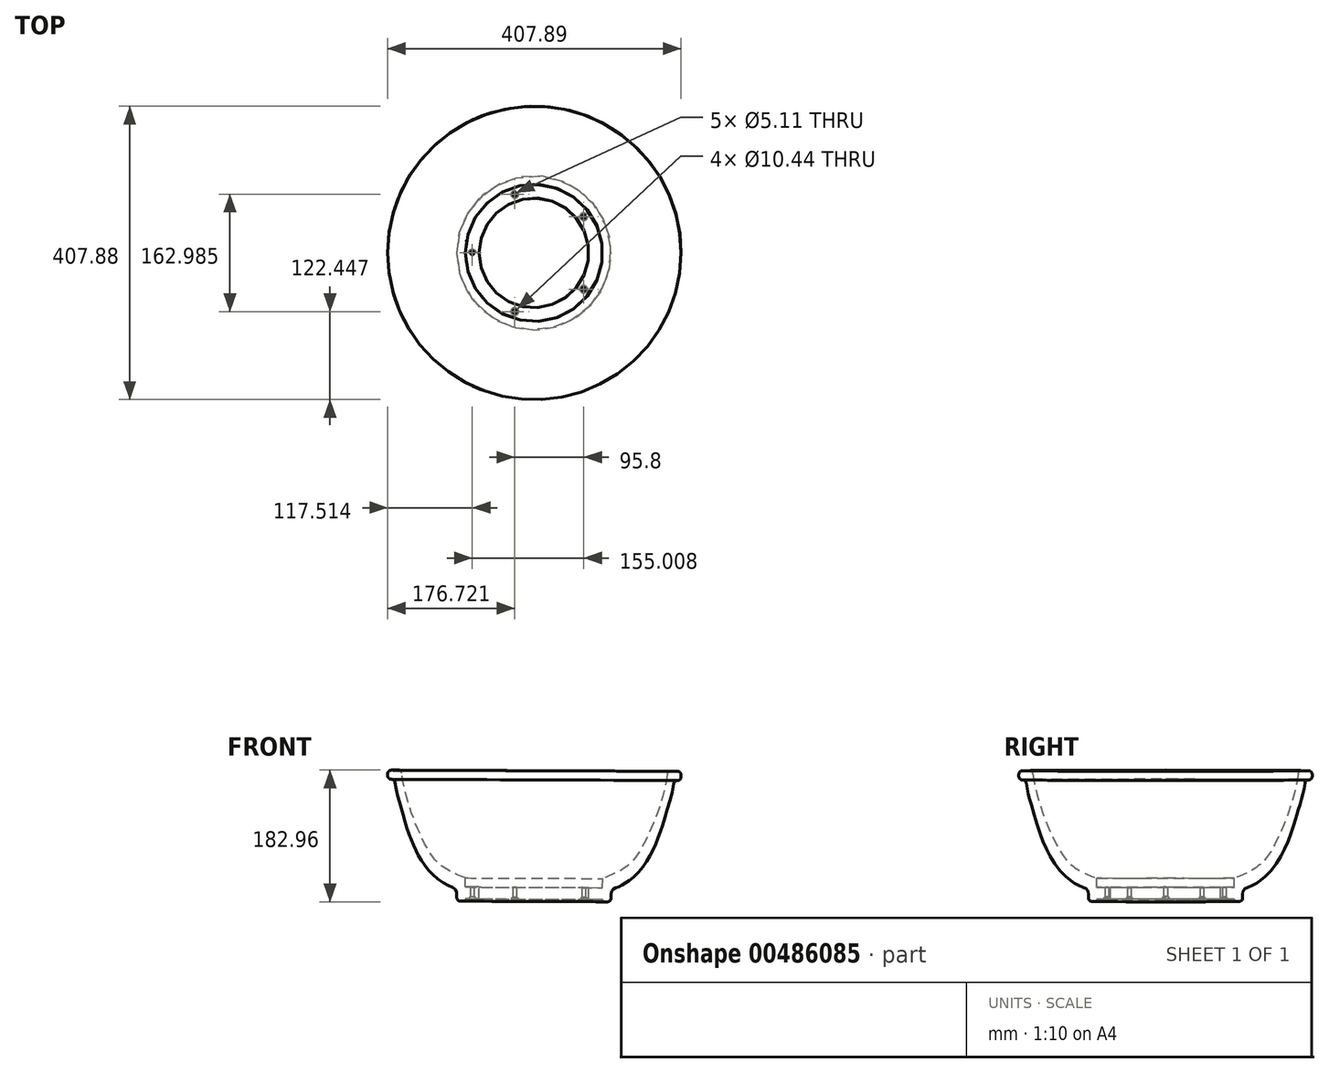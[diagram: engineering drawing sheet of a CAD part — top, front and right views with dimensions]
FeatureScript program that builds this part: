
annotation { "Feature Type Name" : "Feature", "Feature Type Description" : "" }
export const myFeature = defineFeature(function(context is Context, id is Id, definition is map)
    precondition{}
    {
        {
            var Q0;
            Q0=qCreatedBy(makeId("Front.planeOp"),FACE);
            var sketch = newSketch(context, id + "F0", { "sketchPlane" : qUnion([Q0])});
            skLineSegment(sketch, "E0", {"start": v(0, 0) * mm, "end": v(-114.3, 0) * mm, "construction": true});
            skLineSegment(sketch, "E1", {"start": v(0, 0) * mm, "end": v(1.53, 4.69) * mm, "construction": true});
            skLineSegment(sketch, "E2", {"start": v(0, 0) * mm, "end": v(0.77, 180.97) * mm, "construction": true});
            skPoint(sketch, "E2.endSnap0", {"position": v(0.77, 2.34) * mm});
            skLineSegment(sketch, "E3", {"start": v(-76.2, 0) * mm, "end": v(-76.2, 12.7) * mm, "construction": true});
            skLineSegment(sketch, "E4", {"start": v(0.77, 180.97) * mm, "end": v(-177.03, 181.73) * mm, "construction": true});
            skLineSegment(sketch, "E5", {"start": v(-177.03, 181.73) * mm, "end": v(-196.08, 181.73) * mm, "construction": true});
            skLineSegment(sketch, "E6", {"start": v(-196.08, 181.73) * mm, "end": v(-196.08, 169.03) * mm, "construction": true});
            skLineSegment(sketch, "E7", {"start": v(-196.08, 169.03) * mm, "end": v(-186.43, 169.03) * mm, "construction": true});
            skSolve(sketch);
        }
        {
            var Q0;
            Q0=qCreatedBy(makeId("Front.planeOp"),FACE);
            var sketch = newSketch(context, id + "F1", { "sketchPlane" : qUnion([Q0])});
            skLineSegment(sketch, "E8", {"start": v(-76.2, 0) * mm, "end": v(-76.2, 19.05) * mm});
            skLineSegment(sketch, "E9", {"start": v(-76.2, 19.05) * mm, "end": v(-95.25, 19.05) * mm});
            skLineSegment(sketch, "E10", {"start": v(-95.25, 19.05) * mm, "end": v(-95.25, 31.75) * mm});
            skLineSegment(sketch, "E11", {"start": v(-76.2, 0) * mm, "end": v(0, 0) * mm, "construction": true});
            skFitSpline(sketch, "E12", {"points": [v(-95.25, 31.75) * mm, v(-124, 45.57) * mm, v(-142.38, 63.68) * mm, v(-157, 90.58) * mm, v(-171.8, 127.39) * mm, v(-184.15, 181.6) * mm], "startDerivative": vector(-110.55, 41.42) * mm, "endDerivative": vector(-27.24, 248.45) * mm});
            skLineSegment(sketch, "E13", {"start": v(-184.15, 181.6) * mm, "end": v(-203.2, 181.6) * mm});
            skLineSegment(sketch, "E14", {"start": v(-203.2, 181.6) * mm, "end": v(-203.2, 168.9) * mm});
            skLineSegment(sketch, "E15", {"start": v(-203.2, 168.9) * mm, "end": v(-193.55, 168.9) * mm});
            skFitSpline(sketch, "E16", {"points": [v(-107.95, -0.5) * mm, v(-107.95, 14.65) * mm, v(-118.56, 20.96) * mm, v(-145.31, 41.35) * mm, v(-162.26, 66.76) * mm, v(-173.6, 93.1) * mm, v(-185.14, 131) * mm, v(-193.55, 168.9) * mm], "startDerivative": vector(19.18, 91.75) * mm, "endDerivative": vector(-30.73, 264.01) * mm});
            skLineSegment(sketch, "E17", {"start": v(-107.95, -0.5) * mm, "end": v(-95.25, -0.5) * mm});
            skLineSegment(sketch, "E18", {"start": v(-95.25, -0.5) * mm, "end": v(-95.25, 2.75) * mm});
            skLineSegment(sketch, "E19", {"start": v(-95.25, 2.75) * mm, "end": v(-76.2, 2.75) * mm});
            skLineSegment(sketch, "E20", {"start": v(0, 0) * mm, "end": v(0, 5.55) * mm, "construction": true});
            skLineSegment(sketch, "E21", {"start": v(0, 0) * mm, "end": v(0, 186.95) * mm, "construction": true});
            skPoint(sketch, "E22", {"position": v(0, 31.75) * mm});
            skSolve(sketch);
        }
        {
            var Q0;
            Q0=makeQuery(id+"F1.imprint","IMPRINT",FACE,{"disambiguationData":[TD([[makeQuery(id+"F1.imprint","IMPRINT",EDGE,{"derivedFrom":sQuery(id+"F1.wireOp",EDGE,"E8")}),1.0]])]});
            var Q1;
            Q1=sQuery(id+"F0.wireOp",EDGE,"E2");
            revolve(context, id + "F2", {"entities" : qUnion([Q0]), "axis" : qUnion([Q1]), "revolveType" : RevolveType.FULL});
        }
        {
            var Q0;
            Q0=makeQuery(id+"F2.opRevolve","SWEPT_EDGE",EDGE,{"disambiguationData":[OSD([sQuery(id+"F1.wireOp",EDGE,"E13"),sQuery(id+"F1.wireOp",EDGE,"E14")])]});
            var Q1;
            Q1=makeQuery(id+"F2.opRevolve","SWEPT_EDGE",EDGE,{"disambiguationData":[OSD([sQuery(id+"F1.wireOp",EDGE,"E14"),sQuery(id+"F1.wireOp",EDGE,"E15")])]});
            var Q2;
            Q2=makeQuery(id+"F2.opRevolve","SWEPT_EDGE",EDGE,{"disambiguationData":[OSD([sQuery(id+"F1.wireOp",EDGE,"E12"),sQuery(id+"F1.wireOp",EDGE,"E13")])]});
            var Q3;
            Q3=makeQuery(id+"F2.opRevolve","SWEPT_EDGE",EDGE,{"disambiguationData":[OSD([sQuery(id+"F1.wireOp",EDGE,"E15"),sQuery(id+"F1.wireOp",EDGE,"E16")])]});
            fillet(context, id + "F3", {"entities" : qUnion([Q0, Q1, Q2, Q3]), "radius" : 5.08 * mm, "tangentPropagation" : true, "allowEdgeOverflow" : false});
        }
        {
            var Q0;
            Q0=makeQuery(id+"F2.opRevolve","SWEPT_EDGE",EDGE,{"disambiguationData":[OSD([sQuery(id+"F1.wireOp",EDGE,"yEywBuH0-BsC1-ELP2-RhLg-4a1Xm9qmPdDr"),sQuery(id+"F1.wireOp",EDGE,"E16")])]});
            fillet(context, id + "F4", {"entities" : qUnion([Q0]), "radius" : 5.08 * mm, "tangentPropagation" : true, "allowEdgeOverflow" : false});
        }
        {
            var Q0;
            Q0=qCreatedBy(makeId("Top.planeOp"),FACE);
            var sketch = newSketch(context, id + "F5", { "sketchPlane" : qUnion([Q0])});
            skCircle(sketch, "E23", {"center": v(0, 0) * mm, "radius": 85.69 * mm, "construction": true});
            skPoint(sketch, "E24", {"position": v(-85.69, 0) * mm});
            skPoint(sketch, "E25.1.0", {"position": v(-26.48, -81.5) * mm});
            skPoint(sketch, "E25.2.0", {"position": v(69.32, -50.37) * mm});
            skPoint(sketch, "E25.3.0", {"position": v(69.32, 50.37) * mm});
            skPoint(sketch, "E25.4.0", {"position": v(-26.48, 81.5) * mm});
            skSolve(sketch);
        }
        {
            var Q0;
            Q0=sQuery(id+"F5.wireOp",VERTEX,"E24");
            var Q1;
            Q1=sQuery(id+"F5.wireOp",VERTEX,"E25.1.0");
            var Q2;
            Q2=sQuery(id+"F5.wireOp",VERTEX,"E25.2.0");
            var Q3;
            Q3=sQuery(id+"F5.wireOp",VERTEX,"E25.3.0");
            var Q4;
            Q4=sQuery(id+"F5.wireOp",VERTEX,"E25.4.0");
            var Q5;
            Q5=makeQuery(id+"F2.opRevolve","SWEPT_BODY",BODY,{"disambiguationData":[OSD([sQuery(id+"F1.wireOp",EDGE,"E8"),sQuery(id+"F1.wireOp",EDGE,"E9"),sQuery(id+"F1.wireOp",EDGE,"E10"),sQuery(id+"F1.wireOp",EDGE,"E12"),sQuery(id+"F1.wireOp",EDGE,"E13"),sQuery(id+"F1.wireOp",EDGE,"E14"),sQuery(id+"F1.wireOp",EDGE,"E15"),sQuery(id+"F1.wireOp",EDGE,"E16"),sQuery(id+"F1.wireOp",EDGE,"E17"),sQuery(id+"F1.wireOp",EDGE,"E18"),sQuery(id+"F1.wireOp",EDGE,"E19")])]});
            hole(context, id + "F6", {"style" : HoleStyle.C_SINK, "endStyle" : HoleEndStyle.THROUGH, "oppositeDirection" : true, "standardTappedOrClearance" : lookupTablePath({ "standard" : "ANSI", "fit" : "Normal (ASME)", "size" : "#10", "type" : "Clearance" }), "standardBlindInLast" : lookupTablePath({ "fit" : "Free", "standard" : "ANSI", "size" : "#10", "type" : "Clearance" }), "holeDiameter" : 5.1 * mm, "cSinkDiameter" : 10.44 * mm, "cSinkAngle" : 82 * degree, "isTappedThrough" : true, "tappedDepth" : 12.7 * mm, "tapClearance" : 3, "locations" : qUnion([Q0, Q1, Q2, Q3, Q4]), "scope" : qUnion([Q5])});
        }
        {
            var Q0;
            Q0=makeQuery(id+"F2.opRevolve","SWEPT_FACE",FACE,{"disambiguationData":[OSD([sQuery(id+"F1.wireOp",EDGE,"E17")])]});
            fillet(context, id + "F7", {"entities" : qUnion([Q0]), "radius" : 3.25 * mm, "tangentPropagation" : true, "allowEdgeOverflow" : false});
        }
    });
